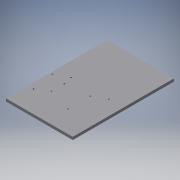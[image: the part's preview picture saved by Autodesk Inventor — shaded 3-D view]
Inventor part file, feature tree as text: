
AUTODESK INVENTOR PART (.ipt)
format: ipt  version: 2019 (Build 230136000, 136)  size: 117,760 bytes
history: native  units: in
note: dims shown in document units (in); Inventor stores cm internally (conversion verified against a paired STEP export)
features: reference x6, sketch x3, other x3, extrude x2, hole x1, projected_geometry x1
ambient origin geometry x8: Origin, YZ Plane, XZ Plane, XY Plane, X Axis, Y Axis, Z Axis, Center Point
bodies: Solid1 (feature_tree)
feature tree (16):
  extrude  "Extrusion1"  Depth=8.6614in
  hole  "Hole1"  [1 undecoded]
  extrude  "Extrusion2"  Depth=0.3937in
  sketch  "Sketch1"  dims[d0=5.7087in d1=8.6614in]
  sketch  "Sketch2"  dims[d2=0.2362in d3=0.0in d4=1.2402in]
  sketch  "Sketch3"  dims[d5=1.2402in d6=4.3307in d7=4.3307in d8=0.1181in d9=0.2953in d10=0.1476in d11=0.0984in d12=90.0deg d13=0.0984in d14=0.0in d15=0.3937in d16=0.0in]
  projected_geometry  "Projected Loop1"
  reference  "Reference7"
  reference  "Reference8"
  reference  "Reference9"
  reference  "Reference10"
  reference  "Reference11"
  reference  "Reference12"
  other  "<userpath>\OneDrive\Documents\Inventor\Assembly1.iam"
  other  "Assembly1.iam"
  other  "arduino mega 2560:1"
note: 1 required parameter value undecoded (feature->parameter linkage not recoverable at this tier; creation-order binding heuristic only, values carry confidence <= 0.55)
